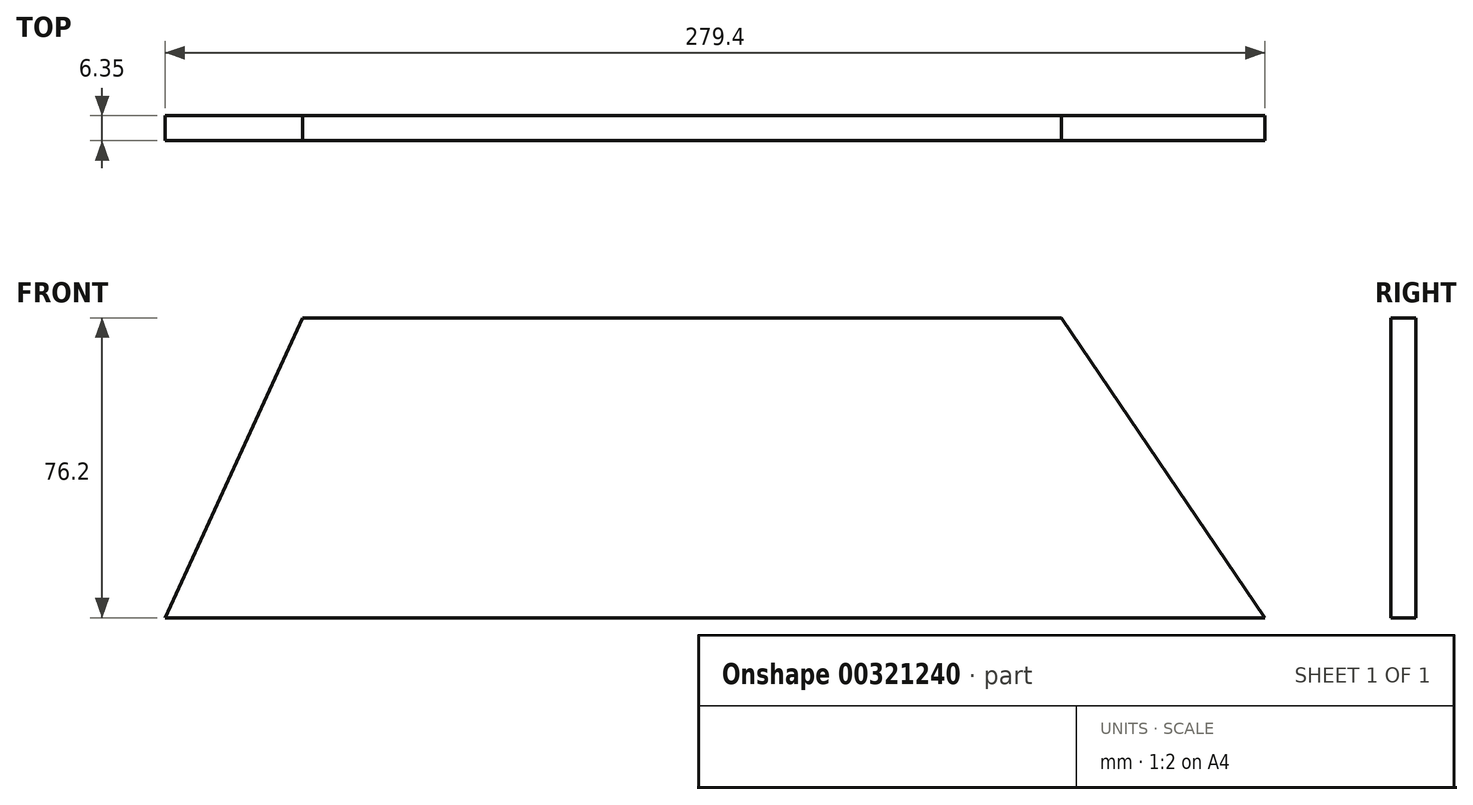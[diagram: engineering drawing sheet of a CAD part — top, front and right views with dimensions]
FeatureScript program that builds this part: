
annotation { "Feature Type Name" : "Feature", "Feature Type Description" : "" }
export const myFeature = defineFeature(function(context is Context, id is Id, definition is map)
    precondition{}
    {
        {
            var Q0;
            Q0=qCreatedBy(makeId("Front.planeOp"),FACE);
            var sketch = newSketch(context, id + "F0", { "sketchPlane" : qUnion([Q0])});
            skLineSegment(sketch, "E0", {"start": v(-138.84, 0) * mm, "end": v(140.56, 0) * mm});
            skLineSegment(sketch, "E1", {"start": v(-138.84, 0) * mm, "end": v(-103.92, 76.2) * mm});
            skLineSegment(sketch, "E2", {"start": v(-103.92, 76.2) * mm, "end": v(-69, 0) * mm});
            skLineSegment(sketch, "E3", {"start": v(-69, 0) * mm, "end": v(-34.07, 76.2) * mm});
            skLineSegment(sketch, "E4", {"start": v(-34.07, 76.2) * mm, "end": v(0, 0) * mm});
            skLineSegment(sketch, "E5", {"start": v(0, 0) * mm, "end": v(20.95, 76.2) * mm});
            skLineSegment(sketch, "E6", {"start": v(20.95, 76.2) * mm, "end": v(74, 0) * mm});
            skLineSegment(sketch, "E7", {"start": v(74, 0) * mm, "end": v(88.85, 76.2) * mm});
            skLineSegment(sketch, "E8", {"start": v(88.85, 76.2) * mm, "end": v(140.56, 0) * mm});
            skLineSegment(sketch, "E9", {"start": v(-103.92, 76.2) * mm, "end": v(88.85, 76.2) * mm});
            skSolve(sketch);
        }
        {
            var Q0;
            Q0 = qSketchRegion(id + "F0", true);
            extrude(context, id + "F1", {"entities" : qUnion([Q0]), "depth" : 6.35 * mm});
        }
    });
